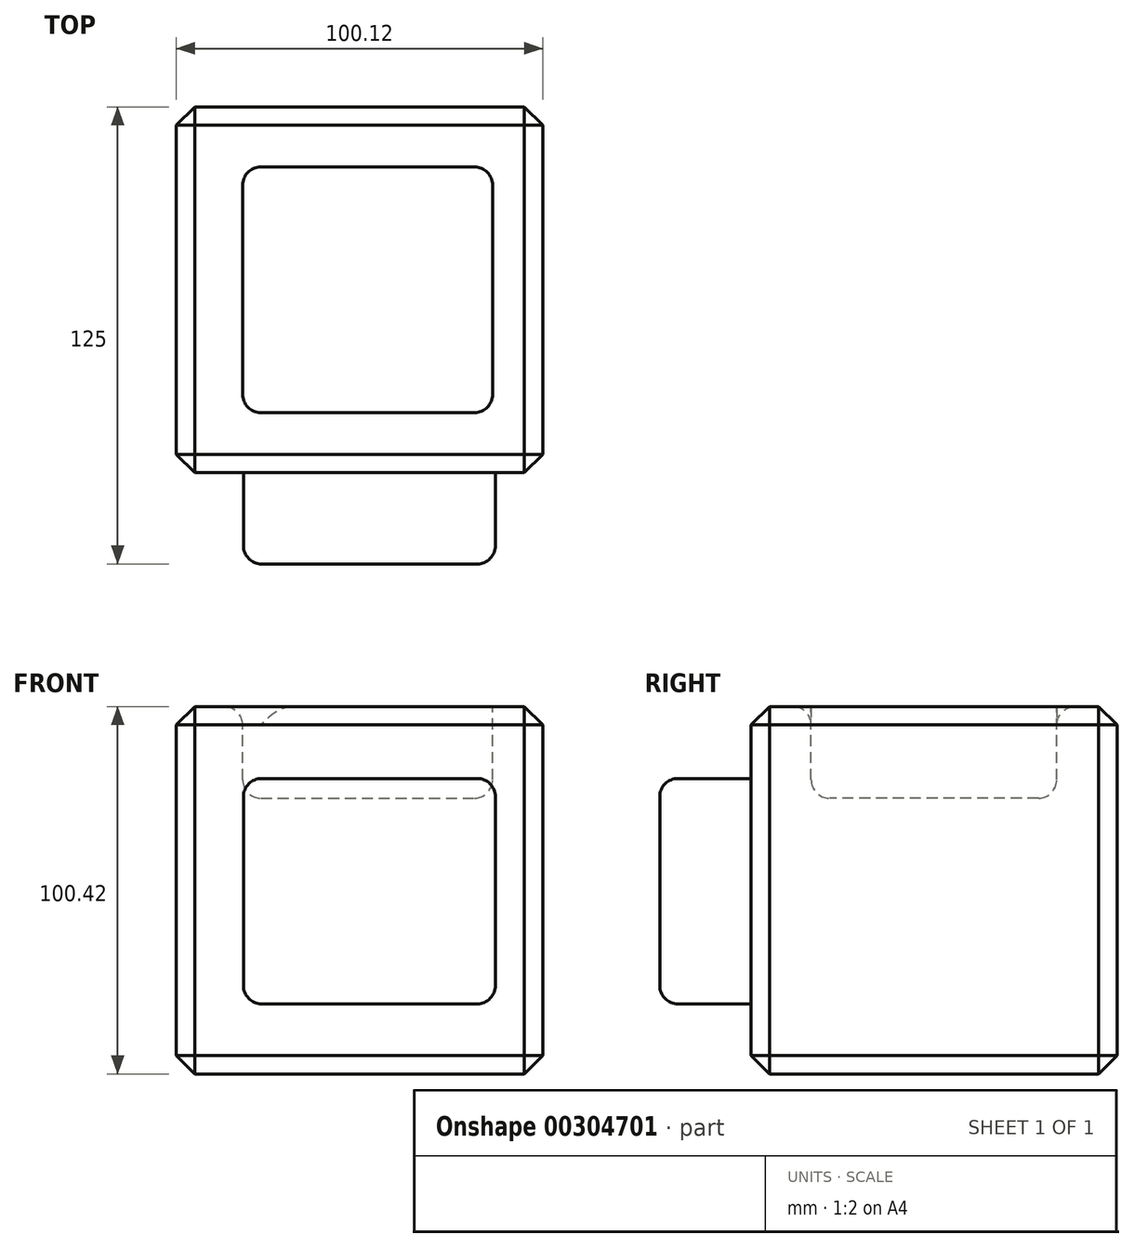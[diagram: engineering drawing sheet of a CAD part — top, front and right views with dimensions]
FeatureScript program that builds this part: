
annotation { "Feature Type Name" : "Feature", "Feature Type Description" : "" }
export const myFeature = defineFeature(function(context is Context, id is Id, definition is map)
    precondition{}
    {
        {
            var Q0;
            Q0=qCreatedBy(makeId("Front.planeOp"),FACE);
            var sketch = newSketch(context, id + "F0", { "sketchPlane" : qUnion([Q0])});
            skLineSegment(sketch, "E0.bottom", {"start": v(-62.88, 35.71) * mm, "end": v(37.24, 35.71) * mm});
            skLineSegment(sketch, "E0.top", {"start": v(-62.88, -64.7) * mm, "end": v(37.24, -64.7) * mm});
            skLineSegment(sketch, "E0.left", {"start": v(-62.88, 35.71) * mm, "end": v(-62.88, -64.7) * mm});
            skLineSegment(sketch, "E0.right", {"start": v(37.24, 35.71) * mm, "end": v(37.24, -64.7) * mm});
            skSolve(sketch);
        }
        {
            var Q0;
            Q0=makeQuery(id+"F0.imprint","IMPRINT",FACE,{"disambiguationData":[TD([[makeQuery(id+"F0.imprint","IMPRINT",EDGE,{"derivedFrom":sQuery(id+"F0.wireOp",EDGE,"E0.bottom")}),-1.0]])]});
            extrude(context, id + "F1", {"entities" : qUnion([Q0]), "depth" : 100 * mm});
        }
        {
            var Q0;
            Q0=makeQuery(id+"F1.opExtrude","SWEPT_EDGE",EDGE,{"disambiguationData":[OSD([sQuery(id+"F0.wireOp",EDGE,"E0.top"),sQuery(id+"F0.wireOp",EDGE,"E0.right")])]});
            var Q1;
            Q1=makeQuery(id+"F1.opExtrude","SWEPT_EDGE",EDGE,{"disambiguationData":[OSD([sQuery(id+"F0.wireOp",EDGE,"E0.bottom"),sQuery(id+"F0.wireOp",EDGE,"E0.left")])]});
            var Q2;
            Q2=makeQuery(id+"F1.opExtrude","CAP_EDGE",EDGE,{"disambiguationData":[OSD([sQuery(id+"F0.wireOp",EDGE,"E0.bottom")])],"isStart":false});
            var Q3;
            Q3=makeQuery(id+"F1.opExtrude","CAP_EDGE",EDGE,{"disambiguationData":[OSD([sQuery(id+"F0.wireOp",EDGE,"E0.bottom")])],"isStart":true});
            var Q4;
            Q4=makeQuery(id+"F1.opExtrude","SWEPT_EDGE",EDGE,{"disambiguationData":[OSD([sQuery(id+"F0.wireOp",EDGE,"E0.bottom"),sQuery(id+"F0.wireOp",EDGE,"E0.right")])]});
            var Q5;
            Q5=makeQuery(id+"F1.opExtrude","CAP_EDGE",EDGE,{"disambiguationData":[OSD([sQuery(id+"F0.wireOp",EDGE,"E0.top")])],"isStart":false});
            var Q6;
            Q6=makeQuery(id+"F1.opExtrude","CAP_EDGE",EDGE,{"disambiguationData":[OSD([sQuery(id+"F0.wireOp",EDGE,"E0.top")])],"isStart":true});
            var Q7;
            Q7=makeQuery(id+"F1.opExtrude","CAP_EDGE",EDGE,{"disambiguationData":[OSD([sQuery(id+"F0.wireOp",EDGE,"E0.left")])],"isStart":false});
            var Q8;
            Q8=makeQuery(id+"F1.opExtrude","SWEPT_EDGE",EDGE,{"disambiguationData":[OSD([sQuery(id+"F0.wireOp",EDGE,"E0.top"),sQuery(id+"F0.wireOp",EDGE,"E0.left")])]});
            var Q9;
            Q9=makeQuery(id+"F1.opExtrude","CAP_EDGE",EDGE,{"disambiguationData":[OSD([sQuery(id+"F0.wireOp",EDGE,"E0.right")])],"isStart":false});
            var Q10;
            Q10=makeQuery(id+"F1.opExtrude","CAP_EDGE",EDGE,{"disambiguationData":[OSD([sQuery(id+"F0.wireOp",EDGE,"E0.left")])],"isStart":true});
            var Q11;
            Q11=makeQuery(id+"F1.opExtrude","CAP_EDGE",EDGE,{"disambiguationData":[OSD([sQuery(id+"F0.wireOp",EDGE,"E0.right")])],"isStart":true});
            chamfer(context, id + "F2", {"entities" : qUnion([Q0, Q1, Q2, Q3, Q4, Q5, Q6, Q7, Q8, Q9, Q10, Q11]), "width" : 5 * mm, "tangentPropagation" : true});
        }
        {
            var Q0;
            Q0=makeQuery(id+"F1.opExtrude","CAP_FACE",FACE,{"disambiguationData":[OSD([sQuery(id+"F0.wireOp",EDGE,"E0.bottom"),sQuery(id+"F0.wireOp",EDGE,"E0.top"),sQuery(id+"F0.wireOp",EDGE,"E0.left"),sQuery(id+"F0.wireOp",EDGE,"E0.right")])],"isStart":false});
            var sketch = newSketch(context, id + "F3", { "sketchPlane" : qUnion([Q0])});
            skLineSegment(sketch, "E1.bottom", {"start": v(-44.54, 16.08) * mm, "end": v(24.34, 16.08) * mm});
            skLineSegment(sketch, "E1.top", {"start": v(-44.54, -45.56) * mm, "end": v(24.34, -45.56) * mm});
            skLineSegment(sketch, "E1.left", {"start": v(-44.54, 16.08) * mm, "end": v(-44.54, -45.56) * mm});
            skLineSegment(sketch, "E1.right", {"start": v(24.34, 16.08) * mm, "end": v(24.34, -45.56) * mm});
            skSolve(sketch);
        }
        {
            var Q0;
            Q0=makeQuery(id+"F3.imprint","IMPRINT",FACE,{"disambiguationData":[TD([[makeQuery(id+"F3.imprint","IMPRINT",EDGE,{"derivedFrom":sQuery(id+"F3.wireOp",EDGE,"E1.bottom")}),-1.0]])]});
            extrude(context, id + "F4", {"entities" : qUnion([Q0]), "operationType" : NewBodyOperationType.ADD, "depth" : 25 * mm});
        }
        {
            var Q0;
            Q0=makeQuery(id+"F4.opExtrude","CAP_EDGE",EDGE,{"disambiguationData":[OSD([sQuery(id+"F3.wireOp",EDGE,"E1.bottom")])],"isStart":false});
            var Q1;
            Q1=makeQuery(id+"F4.opExtrude","CAP_EDGE",EDGE,{"disambiguationData":[OSD([sQuery(id+"F3.wireOp",EDGE,"E1.right")])],"isStart":false});
            var Q2;
            Q2=makeQuery(id+"F4.opExtrude","SWEPT_EDGE",EDGE,{"disambiguationData":[OSD([sQuery(id+"F3.wireOp",EDGE,"E1.bottom"),sQuery(id+"F3.wireOp",EDGE,"E1.right")])]});
            var Q3;
            Q3=makeQuery(id+"F4.opExtrude","SWEPT_EDGE",EDGE,{"disambiguationData":[OSD([sQuery(id+"F3.wireOp",EDGE,"E1.top"),sQuery(id+"F3.wireOp",EDGE,"E1.right")])]});
            var Q4;
            Q4=makeQuery(id+"F4.opExtrude","CAP_EDGE",EDGE,{"disambiguationData":[OSD([sQuery(id+"F3.wireOp",EDGE,"E1.top")])],"isStart":false});
            var Q5;
            Q5=makeQuery(id+"F4.opExtrude","SWEPT_EDGE",EDGE,{"disambiguationData":[OSD([sQuery(id+"F3.wireOp",EDGE,"E1.top"),sQuery(id+"F3.wireOp",EDGE,"E1.left")])]});
            var Q6;
            Q6=makeQuery(id+"F4.opExtrude","CAP_EDGE",EDGE,{"disambiguationData":[OSD([sQuery(id+"F3.wireOp",EDGE,"E1.left")])],"isStart":false});
            var Q7;
            Q7=makeQuery(id+"F4.opExtrude","SWEPT_EDGE",EDGE,{"disambiguationData":[OSD([sQuery(id+"F3.wireOp",EDGE,"E1.bottom"),sQuery(id+"F3.wireOp",EDGE,"E1.left")])]});
            fillet(context, id + "F5", {"entities" : qUnion([Q0, Q1, Q2, Q3, Q4, Q5, Q6, Q7]), "radius" : 5 * mm, "tangentPropagation" : true, "allowEdgeOverflow" : false});
        }
        {
            var Q0;
            Q0=makeQuery(id+"F1.opExtrude","SWEPT_FACE",FACE,{"disambiguationData":[OSD([sQuery(id+"F0.wireOp",EDGE,"E0.bottom")])]});
            var sketch = newSketch(context, id + "F6", { "sketchPlane" : qUnion([Q0])});
            skLineSegment(sketch, "E2.bottom", {"start": v(-44.77, -16.45) * mm, "end": v(23.6, -16.45) * mm});
            skLineSegment(sketch, "E2.top", {"start": v(-44.77, -83.6) * mm, "end": v(23.6, -83.6) * mm});
            skLineSegment(sketch, "E2.left", {"start": v(-44.77, -16.45) * mm, "end": v(-44.77, -83.6) * mm});
            skLineSegment(sketch, "E2.right", {"start": v(23.6, -16.45) * mm, "end": v(23.6, -83.6) * mm});
            skSolve(sketch);
        }
        {
            var Q0;
            Q0=makeQuery(id+"F6.imprint","IMPRINT",FACE,{"disambiguationData":[TD([[makeQuery(id+"F6.imprint","IMPRINT",EDGE,{"derivedFrom":sQuery(id+"F6.wireOp",EDGE,"E2.bottom")}),-1.0]])]});
            extrude(context, id + "F7", {"entities" : qUnion([Q0]), "operationType" : NewBodyOperationType.REMOVE, "oppositeDirection" : true, "depth" : 25 * mm});
        }
        {
            var Q0;
            Q0=makeQuery(id+"F7.boolean.opBoolean","COPY",EDGE,{"derivedFrom":makeQuery(id+"F7.opExtrude","CAP_EDGE",EDGE,{"disambiguationData":[OSD([sQuery(id+"F6.wireOp",EDGE,"E2.bottom")])],"isStart":false})});
            var Q1;
            Q1=makeQuery(id+"F7.boolean.opBoolean","COPY",EDGE,{"derivedFrom":makeQuery(id+"F7.opExtrude","CAP_EDGE",EDGE,{"disambiguationData":[OSD([sQuery(id+"F6.wireOp",EDGE,"E2.left")])],"isStart":false})});
            var Q2;
            Q2=makeQuery(id+"F7.boolean.opBoolean","COPY",EDGE,{"derivedFrom":makeQuery(id+"F7.opExtrude","CAP_EDGE",EDGE,{"disambiguationData":[OSD([sQuery(id+"F6.wireOp",EDGE,"E2.top")])],"isStart":false})});
            var Q3;
            Q3=makeQuery(id+"F7.boolean.opBoolean","COPY",EDGE,{"derivedFrom":makeQuery(id+"F7.opExtrude","CAP_EDGE",EDGE,{"disambiguationData":[OSD([sQuery(id+"F6.wireOp",EDGE,"E2.right")])],"isStart":false})});
            var Q4;
            Q4=makeQuery(id+"F7.boolean.opBoolean","COPY",EDGE,{"derivedFrom":makeQuery(id+"F7.opExtrude","SWEPT_EDGE",EDGE,{"disambiguationData":[OSD([sQuery(id+"F6.wireOp",EDGE,"E2.bottom"),sQuery(id+"F6.wireOp",EDGE,"E2.right")])]})});
            var Q5;
            Q5=makeQuery(id+"F7.boolean.opBoolean","COPY",FACE,{"derivedFrom":makeQuery(id+"F7.opExtrude","SWEPT_FACE",FACE,{"disambiguationData":[OSD([sQuery(id+"F6.wireOp",EDGE,"E2.left")])]})});
            var Q6;
            Q6=makeQuery(id+"F7.boolean.opBoolean","COPY",EDGE,{"derivedFrom":makeQuery(id+"F7.opExtrude","SWEPT_EDGE",EDGE,{"disambiguationData":[OSD([sQuery(id+"F6.wireOp",EDGE,"E2.top"),sQuery(id+"F6.wireOp",EDGE,"E2.left")])]})});
            var Q7;
            Q7=makeQuery(id+"F7.boolean.opBoolean","COPY",EDGE,{"derivedFrom":makeQuery(id+"F7.opExtrude","SWEPT_EDGE",EDGE,{"disambiguationData":[OSD([sQuery(id+"F6.wireOp",EDGE,"E2.top"),sQuery(id+"F6.wireOp",EDGE,"E2.right")])]})});
            fillet(context, id + "F8", {"entities" : qUnion([Q0, Q1, Q2, Q3, Q4, Q5, Q6, Q7]), "radius" : 5 * mm, "tangentPropagation" : true, "allowEdgeOverflow" : false});
        }
    });
